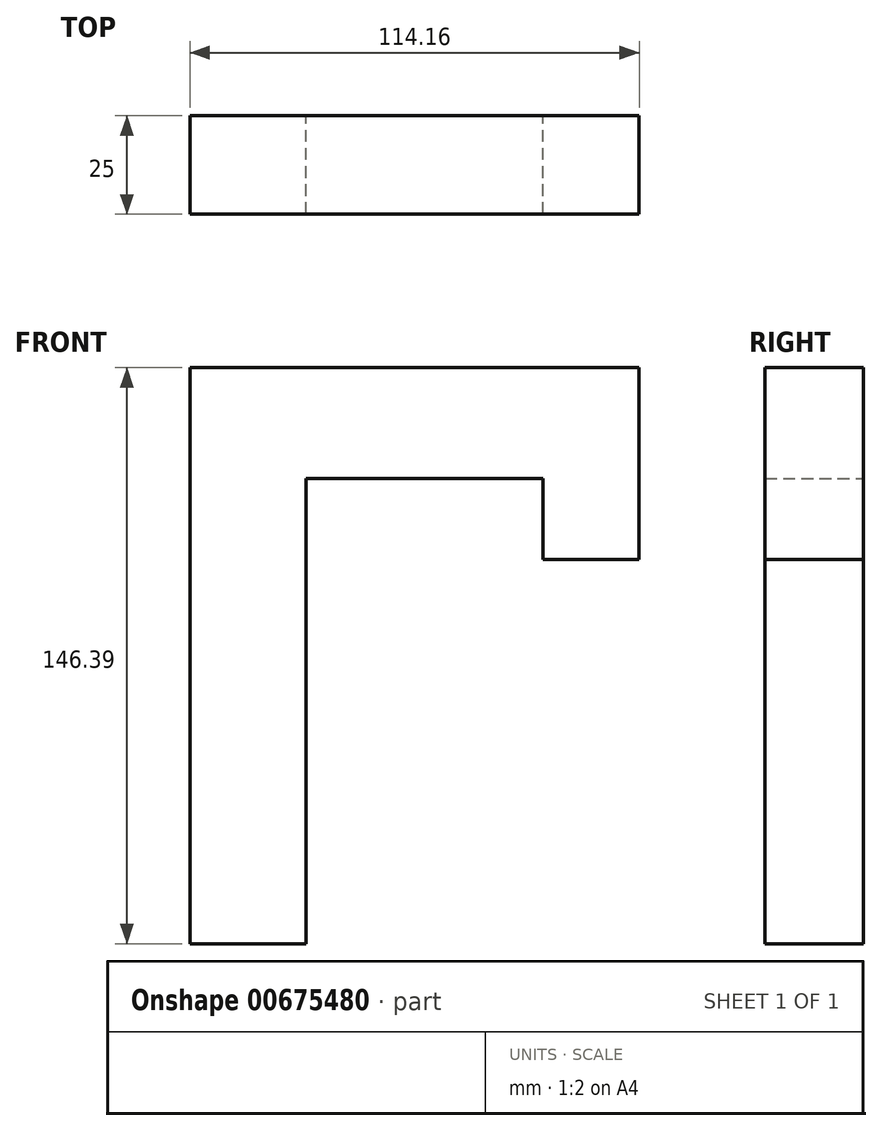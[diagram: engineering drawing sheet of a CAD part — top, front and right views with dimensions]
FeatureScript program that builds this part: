
annotation { "Feature Type Name" : "Feature", "Feature Type Description" : "" }
export const myFeature = defineFeature(function(context is Context, id is Id, definition is map)
    precondition{}
    {
        {
            var Q0;
            Q0=qCreatedBy(makeId("Front.planeOp"),FACE);
            var sketch = newSketch(context, id + "F0", { "sketchPlane" : qUnion([Q0])});
            skLineSegment(sketch, "E0", {"start": v(-74.54, 79.24) * mm, "end": v(24.4, 79.24) * mm});
            skLineSegment(sketch, "E1", {"start": v(24.4, 79.24) * mm, "end": v(24.4, 30.44) * mm});
            skLineSegment(sketch, "E2", {"start": v(24.4, 30.44) * mm, "end": v(0, 30.44) * mm});
            skLineSegment(sketch, "E3", {"start": v(0, 30.44) * mm, "end": v(0, 51.03) * mm});
            skLineSegment(sketch, "E4", {"start": v(0, 51.03) * mm, "end": v(-60.2, 51.03) * mm});
            skLineSegment(sketch, "E5", {"start": v(-60.2, 51.03) * mm, "end": v(-60.2, -67.15) * mm});
            skLineSegment(sketch, "E6", {"start": v(-60.2, -67.15) * mm, "end": v(-89.76, -67.15) * mm});
            skLineSegment(sketch, "E7", {"start": v(-89.76, -67.15) * mm, "end": v(-89.76, 79.24) * mm});
            skLineSegment(sketch, "E8", {"start": v(-89.76, 79.24) * mm, "end": v(-74.54, 79.24) * mm});
            skSolve(sketch);
        }
        {
            var Q0;
            Q0 = qSketchRegion(id + "F0", true);
            extrude(context, id + "F1", {"entities" : qUnion([Q0]), "depth" : 25 * mm, "offsetDistance" : 25 * mm});
        }
    });
